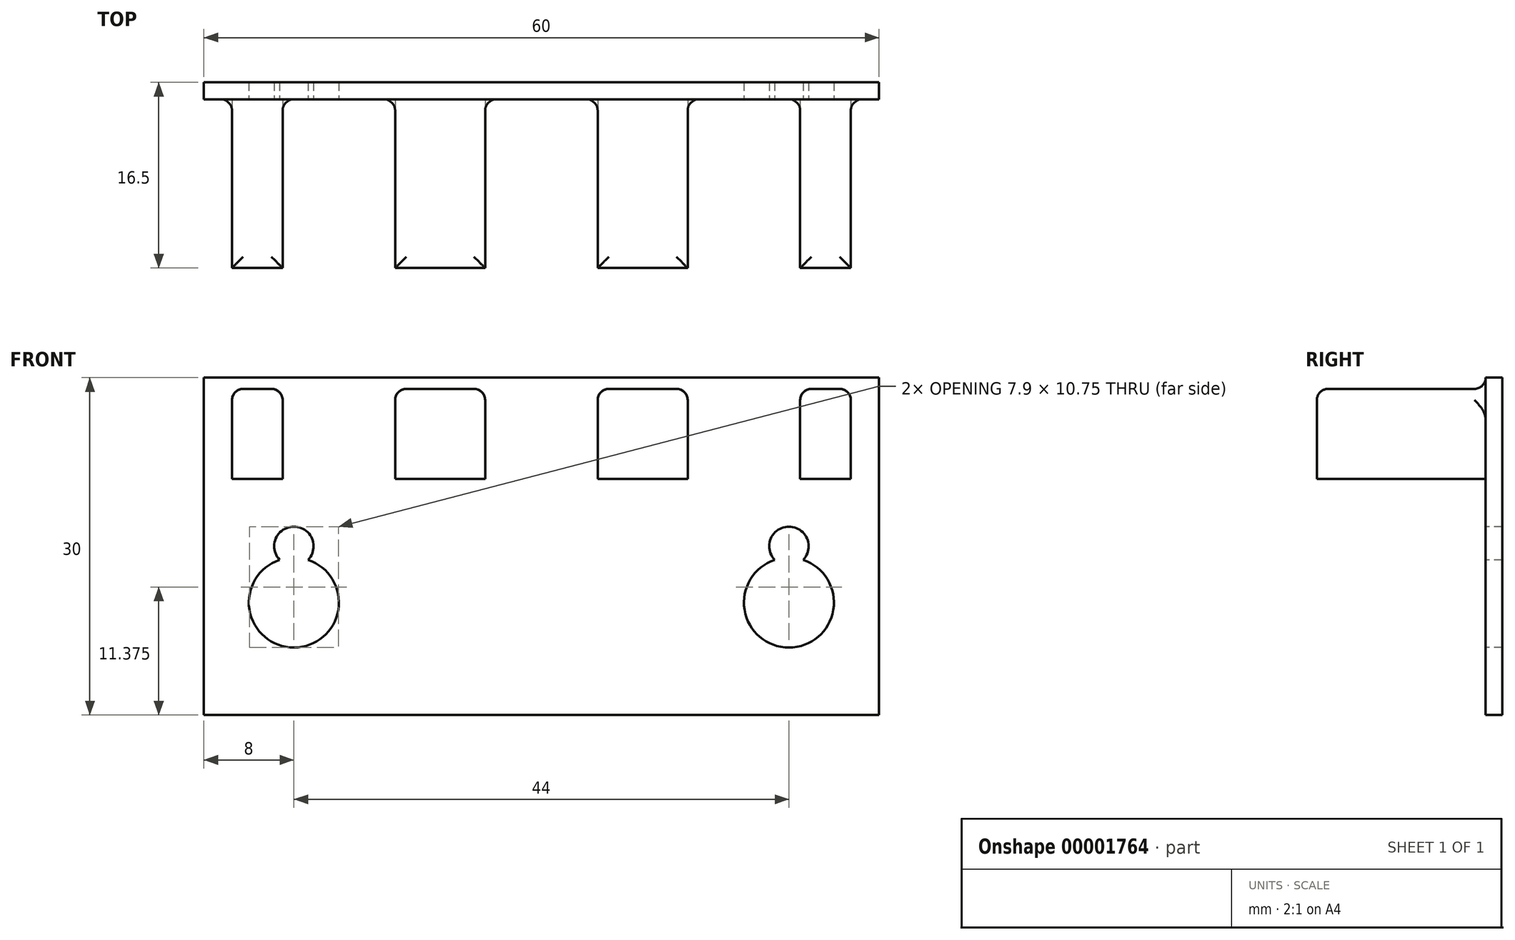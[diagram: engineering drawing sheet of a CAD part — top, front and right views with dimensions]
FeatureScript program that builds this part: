
annotation { "Feature Type Name" : "Feature", "Feature Type Description" : "" }
export const myFeature = defineFeature(function(context is Context, id is Id, definition is map)
    precondition{}
    {
        {
            var Q0;
            Q0=qCreatedBy(makeId("Front.planeOp"),FACE);
            var sketch = newSketch(context, id + "F0", { "sketchPlane" : qUnion([Q0])});
            skLineSegment(sketch, "E0.rect.bottom", {"start": v(30, -15) * mm, "end": v(-30, -15) * mm});
            skLineSegment(sketch, "E0.rect.top", {"start": v(30, 15) * mm, "end": v(-30, 15) * mm});
            skLineSegment(sketch, "E0.rect.left", {"start": v(30, -15) * mm, "end": v(30, 15) * mm});
            skLineSegment(sketch, "E0.rect.right", {"start": v(-30, -15) * mm, "end": v(-30, 15) * mm});
            skPoint(sketch, "E0.rect.middle", {"position": v(0, 0) * mm});
            skSolve(sketch);
        }
        {
            var Q0;
            Q0 = qSketchRegion(id + "F0", true);
            extrude(context, id + "F1", {"entities" : qUnion([Q0]), "depth" : 1.5 * mm});
        }
        {
            var Q0;
            Q0=makeQuery(id+"F1.opExtrude","CAP_FACE",FACE,{"disambiguationData":[OSD([sQuery(id+"F0.wireOp",EDGE,"E0.rect.bottom"),sQuery(id+"F0.wireOp",EDGE,"E0.rect.top"),sQuery(id+"F0.wireOp",EDGE,"E0.rect.left"),sQuery(id+"F0.wireOp",EDGE,"E0.rect.right")])],"isStart":false});
            var sketch = newSketch(context, id + "F2", { "sketchPlane" : qUnion([Q0])});
            skLineSegment(sketch, "E1.rect.bottom", {"start": v(27.5, 6) * mm, "end": v(-27.5, 6) * mm});
            skLineSegment(sketch, "E1.rect.top", {"start": v(27.5, 14) * mm, "end": v(-27.5, 14) * mm});
            skLineSegment(sketch, "E1.rect.left", {"start": v(27.5, 6) * mm, "end": v(27.5, 14) * mm});
            skLineSegment(sketch, "E1.rect.right", {"start": v(-27.5, 6) * mm, "end": v(-27.5, 14) * mm});
            skPoint(sketch, "E1.rect.middle", {"position": v(0, 10) * mm});
            skSolve(sketch);
        }
        {
            var Q0;
            Q0 = qSketchRegion(id + "F2", true);
            extrude(context, id + "F3", {"entities" : qUnion([Q0]), "operationType" : NewBodyOperationType.ADD, "depth" : 15 * mm});
        }
        {
            var Q0;
            Q0=makeQuery(id+"F3.opExtrude","CAP_FACE",FACE,{"disambiguationData":[OSD([sQuery(id+"F2.wireOp",EDGE,"E1.rect.bottom"),sQuery(id+"F2.wireOp",EDGE,"E1.rect.top"),sQuery(id+"F2.wireOp",EDGE,"E1.rect.left"),sQuery(id+"F2.wireOp",EDGE,"E1.rect.right")])],"isStart":false});
            var sketch = newSketch(context, id + "F4", { "sketchPlane" : qUnion([Q0])});
            skLineSegment(sketch, "E2.rect.bottom", {"start": v(-13, 6) * mm, "end": v(-23, 6) * mm});
            skLineSegment(sketch, "E2.rect.top", {"start": v(-13, 14) * mm, "end": v(-23, 14) * mm});
            skLineSegment(sketch, "E2.rect.left", {"start": v(-13, 6) * mm, "end": v(-13, 14) * mm});
            skLineSegment(sketch, "E2.rect.right", {"start": v(-23, 6) * mm, "end": v(-23, 14) * mm});
            skPoint(sketch, "E2.rect.middle", {"position": v(-18, 10) * mm});
            skLineSegment(sketch, "E3.rect.bottom", {"start": v(23, 6) * mm, "end": v(13, 6) * mm});
            skLineSegment(sketch, "E3.rect.top", {"start": v(23, 14) * mm, "end": v(13, 14) * mm});
            skLineSegment(sketch, "E3.rect.left", {"start": v(23, 6) * mm, "end": v(23, 14) * mm});
            skLineSegment(sketch, "E3.rect.right", {"start": v(13, 6) * mm, "end": v(13, 14) * mm});
            skPoint(sketch, "E3.rect.middle", {"position": v(18, 10) * mm});
            skLineSegment(sketch, "E4.rect.bottom", {"start": v(5, 6) * mm, "end": v(-5, 6) * mm});
            skLineSegment(sketch, "E4.rect.top", {"start": v(5, 14) * mm, "end": v(-5, 14) * mm});
            skLineSegment(sketch, "E4.rect.left", {"start": v(5, 6) * mm, "end": v(5, 14) * mm});
            skLineSegment(sketch, "E4.rect.right", {"start": v(-5, 6) * mm, "end": v(-5, 14) * mm});
            skPoint(sketch, "E4.rect.middle", {"position": v(0, 10) * mm});
            skSolve(sketch);
        }
        {
            var Q0;
            Q0 = qSketchRegion(id + "F4", true);
            extrude(context, id + "F5", {"entities" : qUnion([Q0]), "operationType" : NewBodyOperationType.REMOVE, "oppositeDirection" : true, "depth" : 15 * mm});
        }
        {
            var Q0;
            Q0=makeQuery(id+"F5.boolean.opBoolean","MERGE",FACE,{"derivedFrom":[makeQuery(id+"F1.opExtrude","CAP_FACE",FACE,{"disambiguationData":[OSD([sQuery(id+"F0.wireOp",EDGE,"E0.rect.bottom"),sQuery(id+"F0.wireOp",EDGE,"E0.rect.top"),sQuery(id+"F0.wireOp",EDGE,"E0.rect.left"),sQuery(id+"F0.wireOp",EDGE,"E0.rect.right")])],"isStart":false}),makeQuery(id+"F5.opExtrude","CAP_FACE",FACE,{"disambiguationData":[OSD([sQuery(id+"F4.wireOp",EDGE,"E2.rect.bottom"),sQuery(id+"F4.wireOp",EDGE,"E2.rect.top"),sQuery(id+"F4.wireOp",EDGE,"E2.rect.left"),sQuery(id+"F4.wireOp",EDGE,"E2.rect.right")])],"isStart":false}),makeQuery(id+"F5.opExtrude","CAP_FACE",FACE,{"disambiguationData":[OSD([sQuery(id+"F4.wireOp",EDGE,"E3.rect.bottom"),sQuery(id+"F4.wireOp",EDGE,"E3.rect.top"),sQuery(id+"F4.wireOp",EDGE,"E3.rect.left"),sQuery(id+"F4.wireOp",EDGE,"E3.rect.right")])],"isStart":false}),makeQuery(id+"F5.opExtrude","CAP_FACE",FACE,{"disambiguationData":[OSD([sQuery(id+"F4.wireOp",EDGE,"E4.rect.bottom"),sQuery(id+"F4.wireOp",EDGE,"E4.rect.top"),sQuery(id+"F4.wireOp",EDGE,"E4.rect.left"),sQuery(id+"F4.wireOp",EDGE,"E4.rect.right")])],"isStart":false})]});
            var sketch = newSketch(context, id + "F6", { "sketchPlane" : qUnion([Q0])});
            skSolve(sketch);
        }
        {
            var Q0;
            {var subQ15=sQuery(id+"F0.wireOp",EDGE,"E0.rect.bottom");Q0=makeQuery(id+"F6.imprint","IMPRINT",FACE,{"disambiguationData":[TD([[makeQuery(id+"F6.imprint","IMPRINT",EDGE,{"derivedFrom":makeQuery(id+"F1.opExtrude","CAP_EDGE",EDGE,{"disambiguationData":[OSD([subQ15])],"isStart":false})}),-1.0]])]});}
            var sketch = newSketch(context, id + "F7", { "sketchPlane" : qUnion([Q0])});
            skArc(sketch, "E5", {"start": v(-23.27, -1.2) * mm, "mid": v(-22, -9) * mm, "end": v(-20.73, -1.2) * mm});
            skArc(sketch, "E6", {"start": v(-20.73, -1.2) * mm, "mid": v(-22, 1.75) * mm, "end": v(-23.27, -1.2) * mm});
            skLineSegment(sketch, "E7", {"start": v(0, 0) * mm, "end": v(0, -12.34) * mm, "construction": true});
            skArc(sketch, "E8", {"start": v(20.73, -1.2) * mm, "mid": v(22, -9) * mm, "end": v(23.27, -1.2) * mm});
            skArc(sketch, "E9", {"start": v(23.27, -1.2) * mm, "mid": v(22, 1.75) * mm, "end": v(20.73, -1.2) * mm});
            skSolve(sketch);
        }
        {
            var Q0;
            Q0=makeQuery(id+"F7.imprint","IMPRINT",FACE,{"disambiguationData":[TD([[makeQuery(id+"F7.imprint","IMPRINT",EDGE,{"derivedFrom":sQuery(id+"F7.wireOp",EDGE,"E5")}),1.0]])]});
            var Q1;
            Q1=makeQuery(id+"F7.imprint","IMPRINT",FACE,{"disambiguationData":[TD([[makeQuery(id+"F7.imprint","IMPRINT",EDGE,{"derivedFrom":sQuery(id+"F7.wireOp",EDGE,"E8")}),1.0]])]});
            extrude(context, id + "F8", {"entities" : qUnion([Q0, Q1]), "operationType" : NewBodyOperationType.REMOVE, "oppositeDirection" : true, "depth" : 25 * mm});
        }
        {
            var Q0;
            {var subQ0=sQuery(id+"F2.wireOp",EDGE,"E1.rect.top");var subQ2=sQuery(id+"F2.wireOp",EDGE,"E1.rect.right");Q0=makeQuery(id+"F5.boolean.opBoolean","SPLIT",FACE,{"disambiguationData":[TD([makeQuery(id+"F3.opExtrude","SWEPT_FACE",FACE,{"disambiguationData":[OSD([subQ2])]})])],"derivedFrom":makeQuery(id+"F3.opExtrude","SWEPT_FACE",FACE,{"disambiguationData":[OSD([subQ0])]})});}
            var Q1;
            {var subQ0=sQuery(id+"F2.wireOp",EDGE,"E1.rect.top");var subQ2=sQuery(id+"F4.wireOp",EDGE,"E2.rect.left");Q1=makeQuery(id+"F5.boolean.opBoolean","SPLIT",FACE,{"disambiguationData":[TD([makeQuery(id+"F5.opExtrude","SWEPT_FACE",FACE,{"disambiguationData":[OSD([subQ2])]})])],"derivedFrom":makeQuery(id+"F3.opExtrude","SWEPT_FACE",FACE,{"disambiguationData":[OSD([subQ0])]})});}
            var Q2;
            {var subQ0=sQuery(id+"F2.wireOp",EDGE,"E1.rect.top");var subQ2=sQuery(id+"F4.wireOp",EDGE,"E3.rect.right");Q2=makeQuery(id+"F5.boolean.opBoolean","SPLIT",FACE,{"disambiguationData":[TD([makeQuery(id+"F5.opExtrude","SWEPT_FACE",FACE,{"disambiguationData":[OSD([subQ2])]})])],"derivedFrom":makeQuery(id+"F3.opExtrude","SWEPT_FACE",FACE,{"disambiguationData":[OSD([subQ0])]})});}
            var Q3;
            {var subQ0=sQuery(id+"F2.wireOp",EDGE,"E1.rect.top");var subQ2=sQuery(id+"F2.wireOp",EDGE,"E1.rect.left");Q3=makeQuery(id+"F5.boolean.opBoolean","SPLIT",FACE,{"disambiguationData":[TD([makeQuery(id+"F3.opExtrude","SWEPT_FACE",FACE,{"disambiguationData":[OSD([subQ2])]})])],"derivedFrom":makeQuery(id+"F3.opExtrude","SWEPT_FACE",FACE,{"disambiguationData":[OSD([subQ0])]})});}
            fillet(context, id + "F9", {"entities" : qUnion([Q0, Q1, Q2, Q3]), "radius" : 1 * mm, "tangentPropagation" : true, "allowEdgeOverflow" : false});
        }
    });
